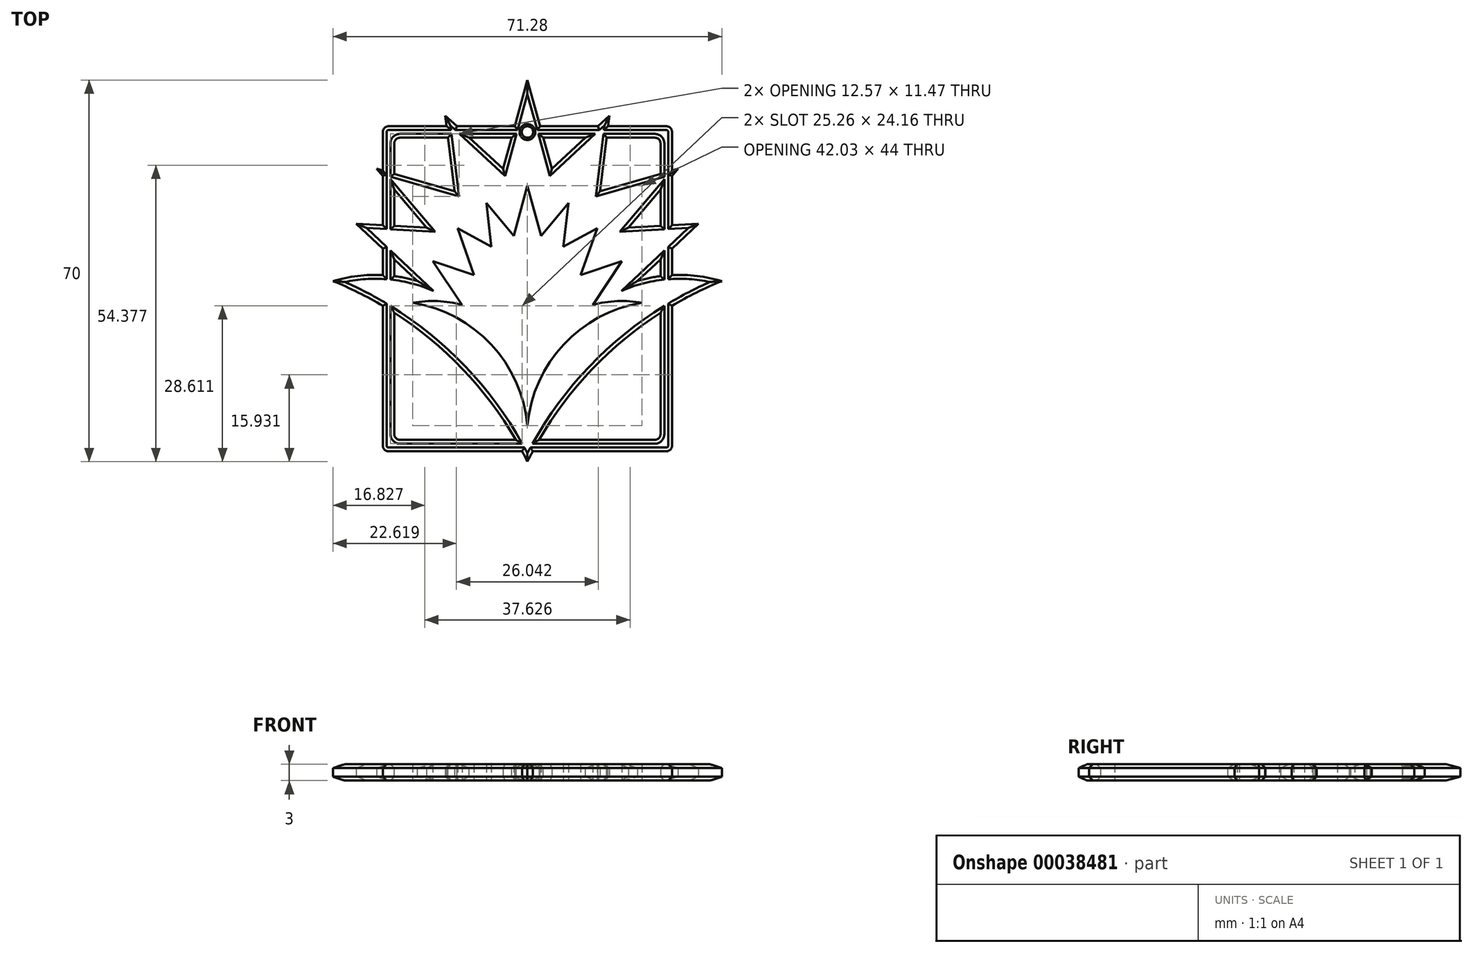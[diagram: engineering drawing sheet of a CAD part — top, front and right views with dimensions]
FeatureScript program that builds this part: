
annotation { "Feature Type Name" : "Feature", "Feature Type Description" : "" }
export const myFeature = defineFeature(function(context is Context, id is Id, definition is map)
    precondition{}
    {
        {
            var Q0;
            Q0=qCreatedBy(makeId("Top.planeOp"),FACE);
            var sketch = newSketch(context, id + "F0", { "sketchPlane" : qUnion([Q0])});
            skLineSegment(sketch, "E0", {"start": v(0, 33.84) * mm, "end": v(0, -36.16) * mm, "construction": true});
            skPoint(sketch, "E1", {"position": v(0, 26.84) * mm});
            skPoint(sketch, "E2", {"position": v(15.04, 27.3) * mm});
            skPoint(sketch, "E3", {"position": v(27.62, 17.57) * mm});
            skPoint(sketch, "E4", {"position": v(31.37, 7.5) * mm});
            skPoint(sketch, "E5", {"position": v(35.64, -3.05) * mm});
            skPoint(sketch, "E6", {"position": v(20.18, -3.02) * mm});
            skPoint(sketch, "E7", {"position": v(18.5, 6.8) * mm});
            skPoint(sketch, "E8", {"position": v(13.35, 13.45) * mm});
            skPoint(sketch, "E9", {"position": v(4.48, 17.54) * mm});
            skLineSegment(sketch, "E10", {"start": v(0, 33.84) * mm, "end": v(4.48, 17.54) * mm});
            skLineSegment(sketch, "E11", {"start": v(15.04, 27.3) * mm, "end": v(13.35, 13.45) * mm});
            skLineSegment(sketch, "E12", {"start": v(15.04, 27.3) * mm, "end": v(4.48, 17.54) * mm});
            skLineSegment(sketch, "E13", {"start": v(13.35, 13.45) * mm, "end": v(27.62, 17.57) * mm});
            skLineSegment(sketch, "E14", {"start": v(27.62, 17.57) * mm, "end": v(18.5, 6.8) * mm});
            skLineSegment(sketch, "E15", {"start": v(18.5, 6.8) * mm, "end": v(31.37, 7.5) * mm});
            skLineSegment(sketch, "E16", {"start": v(31.37, 7.5) * mm, "end": v(20.18, -3.02) * mm});
            skArc(sketch, "E17", {"start": v(35.64, -3.05) * mm, "mid": v(14.77, -16.33) * mm, "end": v(0, -36.16) * mm});
            skArc(sketch, "E18", {"start": v(35.64, -3.05) * mm, "mid": v(27.91, -1.91) * mm, "end": v(20.18, -3.02) * mm});
            skPoint(sketch, "E19.MirrorP", {"position": v(-4.48, 17.54) * mm});
            skPoint(sketch, "E20.MirrorP", {"position": v(-13.35, 13.45) * mm});
            skPoint(sketch, "E21.MirrorP", {"position": v(-15.04, 27.3) * mm});
            skPoint(sketch, "E22.MirrorP", {"position": v(-18.5, 6.8) * mm});
            skPoint(sketch, "E23.MirrorP", {"position": v(-20.18, -3.02) * mm});
            skPoint(sketch, "E24.MirrorP", {"position": v(-31.37, 7.5) * mm});
            skArc(sketch, "E25.MirrorCS", {"start": v(-35.64, -3.05) * mm, "mid": v(-27.91, -1.91) * mm, "end": v(-20.18, -3.02) * mm});
            skLineSegment(sketch, "E26.MirrorCS", {"start": v(0, 33.84) * mm, "end": v(-4.48, 17.54) * mm});
            skPoint(sketch, "E27.MirrorP", {"position": v(-35.64, -3.05) * mm});
            skLineSegment(sketch, "E28.MirrorCS", {"start": v(-15.04, 27.3) * mm, "end": v(-13.35, 13.45) * mm});
            skLineSegment(sketch, "E29.MirrorCS", {"start": v(-31.37, 7.5) * mm, "end": v(-20.18, -3.02) * mm});
            skPoint(sketch, "E30.MirrorP", {"position": v(-27.62, 17.57) * mm});
            skLineSegment(sketch, "E31.MirrorCS", {"start": v(-15.04, 27.3) * mm, "end": v(-4.48, 17.54) * mm});
            skArc(sketch, "E32.MirrorCS", {"start": v(-35.64, -3.05) * mm, "mid": v(-14.77, -16.33) * mm, "end": v(0, -36.16) * mm});
            skLineSegment(sketch, "E33.MirrorCS", {"start": v(-13.35, 13.45) * mm, "end": v(-27.62, 17.57) * mm});
            skLineSegment(sketch, "E34.MirrorCS", {"start": v(-27.62, 17.57) * mm, "end": v(-18.5, 6.8) * mm});
            skLineSegment(sketch, "E35.MirrorCS", {"start": v(-18.5, 6.8) * mm, "end": v(-31.37, 7.5) * mm});
            skSolve(sketch);
        }
        {
            var Q0;
            Q0=qCreatedBy(makeId("Top.planeOp"),FACE);
            var sketch = newSketch(context, id + "F1", { "sketchPlane" : qUnion([Q0])});
            skLineSegment(sketch, "E36", {"start": v(-11.97, -7.42) * mm, "end": v(-17.34, 0.6) * mm});
            skLineSegment(sketch, "E37", {"start": v(-17.34, 0.6) * mm, "end": v(-9.79, -1.93) * mm});
            skLineSegment(sketch, "E38", {"start": v(-9.79, -1.93) * mm, "end": v(-12.8, 6.64) * mm});
            skLineSegment(sketch, "E39", {"start": v(-12.8, 6.64) * mm, "end": v(-6.6, 3.28) * mm});
            skLineSegment(sketch, "E40", {"start": v(-6.6, 3.28) * mm, "end": v(-7.52, 11.26) * mm});
            skLineSegment(sketch, "E41", {"start": v(-7.52, 11.26) * mm, "end": v(-2.5, 5.26) * mm});
            skLineSegment(sketch, "E42", {"start": v(-2.5, 5.26) * mm, "end": v(0, 14.45) * mm});
            skArc(sketch, "E43", {"start": v(0, -29.55) * mm, "mid": v(-6.64, -14.68) * mm, "end": v(-21.02, -7.03) * mm});
            skLineSegment(sketch, "E44.MirrorCS", {"start": v(12.8, 6.64) * mm, "end": v(6.6, 3.28) * mm});
            skLineSegment(sketch, "E45.MirrorCS", {"start": v(6.6, 3.28) * mm, "end": v(7.52, 11.26) * mm});
            skLineSegment(sketch, "E46.MirrorCS", {"start": v(9.79, -1.93) * mm, "end": v(12.8, 6.64) * mm});
            skLineSegment(sketch, "E47.MirrorCS", {"start": v(17.34, 0.6) * mm, "end": v(9.79, -1.93) * mm});
            skLineSegment(sketch, "E48.MirrorCS", {"start": v(2.5, 5.26) * mm, "end": v(0, 14.45) * mm});
            skLineSegment(sketch, "E49.MirrorCS", {"start": v(11.97, -7.42) * mm, "end": v(17.34, 0.6) * mm});
            skLineSegment(sketch, "E50.MirrorCS", {"start": v(7.52, 11.26) * mm, "end": v(2.5, 5.26) * mm});
            skArc(sketch, "E51.MirrorCS", {"start": v(0, -29.55) * mm, "mid": v(6.64, -14.68) * mm, "end": v(21.02, -7.03) * mm});
            skArc(sketch, "E52", {"start": v(-11.97, -7.42) * mm, "mid": v(-16.47, -6.71) * mm, "end": v(-21.02, -7.03) * mm});
            skArc(sketch, "E53.MirrorCS", {"start": v(11.97, -7.42) * mm, "mid": v(16.47, -6.71) * mm, "end": v(21.02, -7.03) * mm});
            skSolve(sketch);
        }
        {
            var Q0;
            Q0=makeQuery(id+"F0.imprint","IMPRINT",FACE,{"disambiguationData":[TD([[makeQuery(id+"F0.imprint","IMPRINT",EDGE,{"derivedFrom":sQuery(id+"F0.wireOp",EDGE,"E10")}),-1.0]])]});
            extrude(context, id + "F2", {"entities" : qUnion([Q0]), "depth" : 3 * mm});
        }
        {
            var Q0;
            Q0=makeQuery(id+"F1.imprint","IMPRINT",FACE,{"disambiguationData":[TD([[makeQuery(id+"F1.imprint","IMPRINT",EDGE,{"derivedFrom":sQuery(id+"F1.wireOp",EDGE,"E36")}),-1.0]])]});
            extrude(context, id + "F3", {"entities" : qUnion([Q0]), "operationType" : NewBodyOperationType.REMOVE, "endBound" : BoundingType.UP_TO_NEXT, "depth" : 25 * mm});
        }
        {
            var Q0;
            Q0=qCreatedBy(makeId("Top.planeOp"),FACE);
            var sketch = newSketch(context, id + "F4", { "sketchPlane" : qUnion([Q0])});
            skLineSegment(sketch, "E54.bottom", {"start": v(-25.5, 25.35) * mm, "end": v(25.5, 25.35) * mm});
            skLineSegment(sketch, "E54.top", {"start": v(-25.5, -34.26) * mm, "end": v(25.5, -34.26) * mm});
            skLineSegment(sketch, "E54.left", {"start": v(-26.5, 24.35) * mm, "end": v(-26.5, -33.26) * mm});
            skLineSegment(sketch, "E54.right", {"start": v(26.5, 24.35) * mm, "end": v(26.5, -33.26) * mm});
            skPoint(sketch, "E55", {"position": v(0, 25.35) * mm});
            skLineSegment(sketch, "E56.0", {"start": v(24.4, 22.25) * mm, "end": v(24.4, -31.16) * mm});
            skLineSegment(sketch, "E56.1", {"start": v(-23.4, 23.25) * mm, "end": v(23.4, 23.25) * mm});
            skLineSegment(sketch, "E56.2", {"start": v(-24.4, 22.25) * mm, "end": v(-24.4, -31.16) * mm});
            skLineSegment(sketch, "E56.3", {"start": v(-23.4, -32.16) * mm, "end": v(23.4, -32.16) * mm});
            skPoint(sketch, "E57.visualSharp", {"position": v(-26.5, 25.35) * mm});
            skArc(sketch, "E57.filletArc", {"start": v(-25.5, 25.35) * mm, "mid": v(-26.2, 25.06) * mm, "end": v(-26.5, 24.35) * mm});
            skPoint(sketch, "E58.visualSharp", {"position": v(-24.4, 23.25) * mm});
            skArc(sketch, "E58.filletArc", {"start": v(-23.4, 23.25) * mm, "mid": v(-24.1, 22.96) * mm, "end": v(-24.4, 22.25) * mm});
            skPoint(sketch, "E59.visualSharp", {"position": v(-26.5, -34.26) * mm});
            skArc(sketch, "E59.filletArc", {"start": v(-26.5, -33.26) * mm, "mid": v(-26.2, -33.97) * mm, "end": v(-25.5, -34.26) * mm});
            skPoint(sketch, "E60.visualSharp", {"position": v(-24.4, -32.16) * mm});
            skArc(sketch, "E60.filletArc", {"start": v(-24.4, -31.16) * mm, "mid": v(-24.1, -31.87) * mm, "end": v(-23.4, -32.16) * mm});
            skPoint(sketch, "E61.visualSharp", {"position": v(24.4, -32.16) * mm});
            skArc(sketch, "E61.filletArc", {"start": v(23.4, -32.16) * mm, "mid": v(24.1, -31.87) * mm, "end": v(24.4, -31.16) * mm});
            skPoint(sketch, "E62.visualSharp", {"position": v(26.5, -34.26) * mm});
            skArc(sketch, "E62.filletArc", {"start": v(25.5, -34.26) * mm, "mid": v(26.2, -33.97) * mm, "end": v(26.5, -33.26) * mm});
            skPoint(sketch, "E63.visualSharp", {"position": v(24.4, 23.25) * mm});
            skArc(sketch, "E63.filletArc", {"start": v(24.4, 22.25) * mm, "mid": v(24.1, 22.96) * mm, "end": v(23.4, 23.25) * mm});
            skPoint(sketch, "E64.visualSharp", {"position": v(26.5, 25.35) * mm});
            skArc(sketch, "E64.filletArc", {"start": v(26.5, 24.35) * mm, "mid": v(26.2, 25.06) * mm, "end": v(25.5, 25.35) * mm});
            skSolve(sketch);
        }
        {
            var Q0;
            Q0=makeQuery(id+"F4.imprint","IMPRINT",FACE,{"disambiguationData":[TD([[makeQuery(id+"F4.imprint","IMPRINT",EDGE,{"derivedFrom":sQuery(id+"F4.wireOp",EDGE,"E54.bottom")}),-1.0]])]});
            var Q1;
            Q1=makeQuery(id+"F2.opExtrude","CAP_FACE",FACE,{"disambiguationData":[OSD([sQuery(id+"F0.wireOp",EDGE,"E10"),sQuery(id+"F0.wireOp",EDGE,"E11"),sQuery(id+"F0.wireOp",EDGE,"E12"),sQuery(id+"F0.wireOp",EDGE,"E13"),sQuery(id+"F0.wireOp",EDGE,"E14"),sQuery(id+"F0.wireOp",EDGE,"E15"),sQuery(id+"F0.wireOp",EDGE,"E16"),sQuery(id+"F0.wireOp",EDGE,"E17"),sQuery(id+"F0.wireOp",EDGE,"E18"),sQuery(id+"F0.wireOp",EDGE,"E25.MirrorCS"),sQuery(id+"F0.wireOp",EDGE,"E26.MirrorCS"),sQuery(id+"F0.wireOp",EDGE,"E28.MirrorCS"),sQuery(id+"F0.wireOp",EDGE,"E29.MirrorCS"),sQuery(id+"F0.wireOp",EDGE,"E31.MirrorCS"),sQuery(id+"F0.wireOp",EDGE,"E32.MirrorCS"),sQuery(id+"F0.wireOp",EDGE,"E33.MirrorCS"),sQuery(id+"F0.wireOp",EDGE,"E34.MirrorCS"),sQuery(id+"F0.wireOp",EDGE,"E35.MirrorCS")])],"isStart":false});
            extrude(context, id + "F5", {"entities" : qUnion([Q0]), "endBound" : BoundingType.UP_TO_SURFACE, "endBoundEntityFace" : qUnion([Q1]), "depth" : 25 * mm});
        }
        {
            var Q0;
            Q0=makeQuery(id+"F5.opExtrude","CAP_FACE",FACE,{"disambiguationData":[OSD([sQuery(id+"F4.wireOp",EDGE,"E54.bottom"),sQuery(id+"F4.wireOp",EDGE,"E54.top"),sQuery(id+"F4.wireOp",EDGE,"E54.left"),sQuery(id+"F4.wireOp",EDGE,"E54.right"),sQuery(id+"F4.wireOp",EDGE,"E56.0"),sQuery(id+"F4.wireOp",EDGE,"E56.1"),sQuery(id+"F4.wireOp",EDGE,"E56.2"),sQuery(id+"F4.wireOp",EDGE,"E56.3")])],"isStart":false});
            var Q1;
            Q1=makeQuery(id+"F5.opExtrude","CAP_FACE",FACE,{"disambiguationData":[OSD([sQuery(id+"F4.wireOp",EDGE,"E54.bottom"),sQuery(id+"F4.wireOp",EDGE,"E54.top"),sQuery(id+"F4.wireOp",EDGE,"E54.left"),sQuery(id+"F4.wireOp",EDGE,"E54.right"),sQuery(id+"F4.wireOp",EDGE,"E56.0"),sQuery(id+"F4.wireOp",EDGE,"E56.1"),sQuery(id+"F4.wireOp",EDGE,"E56.2"),sQuery(id+"F4.wireOp",EDGE,"E56.3")])],"isStart":true});
            chamfer(context, id + "F6", {"entities" : qUnion([Q0, Q1]), "width" : 0.7 * mm, "tangentPropagation" : true});
        }
        {
            var Q0;
            Q0=makeQuery(id+"F2.opExtrude","CAP_EDGE",EDGE,{"disambiguationData":[OSD([sQuery(id+"F0.wireOp",EDGE,"E32.MirrorCS")])],"isStart":false});
            var Q1;
            Q1=makeQuery(id+"F2.opExtrude","CAP_EDGE",EDGE,{"disambiguationData":[OSD([sQuery(id+"F0.wireOp",EDGE,"E25.MirrorCS")])],"isStart":false});
            var Q2;
            Q2=makeQuery(id+"F2.opExtrude","CAP_EDGE",EDGE,{"disambiguationData":[OSD([sQuery(id+"F0.wireOp",EDGE,"E29.MirrorCS")])],"isStart":false});
            var Q3;
            Q3=makeQuery(id+"F2.opExtrude","CAP_EDGE",EDGE,{"disambiguationData":[OSD([sQuery(id+"F0.wireOp",EDGE,"E35.MirrorCS")])],"isStart":false});
            var Q4;
            Q4=makeQuery(id+"F2.opExtrude","CAP_EDGE",EDGE,{"disambiguationData":[OSD([sQuery(id+"F0.wireOp",EDGE,"E34.MirrorCS")])],"isStart":false});
            var Q5;
            Q5=makeQuery(id+"F2.opExtrude","CAP_EDGE",EDGE,{"disambiguationData":[OSD([sQuery(id+"F0.wireOp",EDGE,"E33.MirrorCS")])],"isStart":false});
            var Q6;
            Q6=makeQuery(id+"F2.opExtrude","CAP_EDGE",EDGE,{"disambiguationData":[OSD([sQuery(id+"F0.wireOp",EDGE,"E28.MirrorCS")])],"isStart":false});
            var Q7;
            Q7=makeQuery(id+"F2.opExtrude","CAP_EDGE",EDGE,{"disambiguationData":[OSD([sQuery(id+"F0.wireOp",EDGE,"E31.MirrorCS")])],"isStart":false});
            var Q8;
            Q8=makeQuery(id+"F2.opExtrude","CAP_EDGE",EDGE,{"disambiguationData":[OSD([sQuery(id+"F0.wireOp",EDGE,"E26.MirrorCS")])],"isStart":false});
            var Q9;
            Q9=makeQuery(id+"F2.opExtrude","CAP_EDGE",EDGE,{"disambiguationData":[OSD([sQuery(id+"F0.wireOp",EDGE,"E10")])],"isStart":false});
            var Q10;
            Q10=makeQuery(id+"F2.opExtrude","CAP_EDGE",EDGE,{"disambiguationData":[OSD([sQuery(id+"F0.wireOp",EDGE,"E12")])],"isStart":false});
            var Q11;
            Q11=makeQuery(id+"F2.opExtrude","CAP_EDGE",EDGE,{"disambiguationData":[OSD([sQuery(id+"F0.wireOp",EDGE,"E11")])],"isStart":false});
            var Q12;
            Q12=makeQuery(id+"F2.opExtrude","CAP_EDGE",EDGE,{"disambiguationData":[OSD([sQuery(id+"F0.wireOp",EDGE,"E13")])],"isStart":false});
            var Q13;
            Q13=makeQuery(id+"F2.opExtrude","CAP_EDGE",EDGE,{"disambiguationData":[OSD([sQuery(id+"F0.wireOp",EDGE,"E14")])],"isStart":false});
            var Q14;
            Q14=makeQuery(id+"F2.opExtrude","CAP_EDGE",EDGE,{"disambiguationData":[OSD([sQuery(id+"F0.wireOp",EDGE,"E15")])],"isStart":false});
            var Q15;
            Q15=makeQuery(id+"F2.opExtrude","CAP_EDGE",EDGE,{"disambiguationData":[OSD([sQuery(id+"F0.wireOp",EDGE,"E16")])],"isStart":false});
            var Q16;
            Q16=makeQuery(id+"F2.opExtrude","CAP_EDGE",EDGE,{"disambiguationData":[OSD([sQuery(id+"F0.wireOp",EDGE,"E18")])],"isStart":false});
            var Q17;
            Q17=makeQuery(id+"F2.opExtrude","CAP_EDGE",EDGE,{"disambiguationData":[OSD([sQuery(id+"F0.wireOp",EDGE,"E17")])],"isStart":false});
            chamfer(context, id + "F7", {"entities" : qUnion([Q0, Q1, Q2, Q3, Q4, Q5, Q6, Q7, Q8, Q9, Q10, Q11, Q12, Q13, Q14, Q15, Q16, Q17]), "width" : 0.7 * mm});
        }
        {
            var Q0;
            Q0=makeQuery(id+"F2.opExtrude","CAP_EDGE",EDGE,{"disambiguationData":[OSD([sQuery(id+"F0.wireOp",EDGE,"E17")])],"isStart":true});
            var Q1;
            Q1=makeQuery(id+"F2.opExtrude","CAP_EDGE",EDGE,{"disambiguationData":[OSD([sQuery(id+"F0.wireOp",EDGE,"E18")])],"isStart":true});
            var Q2;
            Q2=makeQuery(id+"F2.opExtrude","CAP_EDGE",EDGE,{"disambiguationData":[OSD([sQuery(id+"F0.wireOp",EDGE,"E16")])],"isStart":true});
            var Q3;
            Q3=makeQuery(id+"F2.opExtrude","CAP_EDGE",EDGE,{"disambiguationData":[OSD([sQuery(id+"F0.wireOp",EDGE,"E15")])],"isStart":true});
            var Q4;
            Q4=makeQuery(id+"F2.opExtrude","CAP_EDGE",EDGE,{"disambiguationData":[OSD([sQuery(id+"F0.wireOp",EDGE,"E14")])],"isStart":true});
            var Q5;
            Q5=makeQuery(id+"F2.opExtrude","CAP_EDGE",EDGE,{"disambiguationData":[OSD([sQuery(id+"F0.wireOp",EDGE,"E13")])],"isStart":true});
            var Q6;
            Q6=makeQuery(id+"F2.opExtrude","CAP_EDGE",EDGE,{"disambiguationData":[OSD([sQuery(id+"F0.wireOp",EDGE,"E11")])],"isStart":true});
            var Q7;
            Q7=makeQuery(id+"F2.opExtrude","CAP_EDGE",EDGE,{"disambiguationData":[OSD([sQuery(id+"F0.wireOp",EDGE,"E12")])],"isStart":true});
            var Q8;
            Q8=makeQuery(id+"F2.opExtrude","CAP_EDGE",EDGE,{"disambiguationData":[OSD([sQuery(id+"F0.wireOp",EDGE,"E10")])],"isStart":true});
            var Q9;
            Q9=makeQuery(id+"F2.opExtrude","CAP_EDGE",EDGE,{"disambiguationData":[OSD([sQuery(id+"F0.wireOp",EDGE,"E26.MirrorCS")])],"isStart":true});
            var Q10;
            Q10=makeQuery(id+"F2.opExtrude","CAP_EDGE",EDGE,{"disambiguationData":[OSD([sQuery(id+"F0.wireOp",EDGE,"E31.MirrorCS")])],"isStart":true});
            var Q11;
            Q11=makeQuery(id+"F2.opExtrude","CAP_EDGE",EDGE,{"disambiguationData":[OSD([sQuery(id+"F0.wireOp",EDGE,"E28.MirrorCS")])],"isStart":true});
            var Q12;
            Q12=makeQuery(id+"F2.opExtrude","CAP_EDGE",EDGE,{"disambiguationData":[OSD([sQuery(id+"F0.wireOp",EDGE,"E33.MirrorCS")])],"isStart":true});
            var Q13;
            Q13=makeQuery(id+"F2.opExtrude","CAP_EDGE",EDGE,{"disambiguationData":[OSD([sQuery(id+"F0.wireOp",EDGE,"E34.MirrorCS")])],"isStart":true});
            var Q14;
            Q14=makeQuery(id+"F2.opExtrude","CAP_EDGE",EDGE,{"disambiguationData":[OSD([sQuery(id+"F0.wireOp",EDGE,"E35.MirrorCS")])],"isStart":true});
            var Q15;
            Q15=makeQuery(id+"F2.opExtrude","CAP_EDGE",EDGE,{"disambiguationData":[OSD([sQuery(id+"F0.wireOp",EDGE,"E29.MirrorCS")])],"isStart":true});
            var Q16;
            Q16=makeQuery(id+"F2.opExtrude","CAP_EDGE",EDGE,{"disambiguationData":[OSD([sQuery(id+"F0.wireOp",EDGE,"E25.MirrorCS")])],"isStart":true});
            var Q17;
            Q17=makeQuery(id+"F2.opExtrude","CAP_EDGE",EDGE,{"disambiguationData":[OSD([sQuery(id+"F0.wireOp",EDGE,"E32.MirrorCS")])],"isStart":true});
            chamfer(context, id + "F8", {"entities" : qUnion([Q0, Q1, Q2, Q3, Q4, Q5, Q6, Q7, Q8, Q9, Q10, Q11, Q12, Q13, Q14, Q15, Q16, Q17]), "width" : 0.7 * mm, "tangentPropagation" : true});
        }
        {
            var Q0;
            Q0=makeQuery(id+"F2.opExtrude","SWEPT_BODY",BODY,{"disambiguationData":[OSD([sQuery(id+"F0.wireOp",EDGE,"E10"),sQuery(id+"F0.wireOp",EDGE,"E11"),sQuery(id+"F0.wireOp",EDGE,"E12"),sQuery(id+"F0.wireOp",EDGE,"E13"),sQuery(id+"F0.wireOp",EDGE,"E14"),sQuery(id+"F0.wireOp",EDGE,"E15"),sQuery(id+"F0.wireOp",EDGE,"E16"),sQuery(id+"F0.wireOp",EDGE,"E17"),sQuery(id+"F0.wireOp",EDGE,"E18"),sQuery(id+"F0.wireOp",EDGE,"E25.MirrorCS"),sQuery(id+"F0.wireOp",EDGE,"E26.MirrorCS"),sQuery(id+"F0.wireOp",EDGE,"E28.MirrorCS"),sQuery(id+"F0.wireOp",EDGE,"E29.MirrorCS"),sQuery(id+"F0.wireOp",EDGE,"E31.MirrorCS"),sQuery(id+"F0.wireOp",EDGE,"E32.MirrorCS"),sQuery(id+"F0.wireOp",EDGE,"E33.MirrorCS"),sQuery(id+"F0.wireOp",EDGE,"E34.MirrorCS"),sQuery(id+"F0.wireOp",EDGE,"E35.MirrorCS")])]});
            var Q1;
            Q1=makeQuery(id+"F5.opExtrude","SWEPT_BODY",BODY,{"disambiguationData":[OSD([sQuery(id+"F4.wireOp",EDGE,"E54.bottom"),sQuery(id+"F4.wireOp",EDGE,"E54.top"),sQuery(id+"F4.wireOp",EDGE,"E54.left"),sQuery(id+"F4.wireOp",EDGE,"E54.right"),sQuery(id+"F4.wireOp",EDGE,"E56.0"),sQuery(id+"F4.wireOp",EDGE,"E56.1"),sQuery(id+"F4.wireOp",EDGE,"E56.2"),sQuery(id+"F4.wireOp",EDGE,"E56.3")])]});
            booleanBodies(context, id + "F9", {"operationType" : BooleanOperationType.UNION, "tools" : qUnion([Q0, Q1])});
        }
        {
            var Q0;
            Q0=qCreatedBy(makeId("Top.planeOp"),FACE);
            var sketch = newSketch(context, id + "F10", { "sketchPlane" : qUnion([Q0])});
            skCircle(sketch, "E65", {"center": v(0, 24.3) * mm, "radius": 1.05 * mm});
            skLineSegment(sketch, "E66.0", {"start": v(-25.5, 25.35) * mm, "end": v(25.5, 25.35) * mm, "construction": true});
            skLineSegment(sketch, "E66.1", {"start": v(-23.4, 23.25) * mm, "end": v(23.4, 23.25) * mm, "construction": true});
            skLineSegment(sketch, "E67", {"start": v(0, 25.35) * mm, "end": v(0, 23.25) * mm, "construction": true});
            skSolve(sketch);
        }
        {
            var Q0;
            Q0 = qSketchRegion(id + "F10", true);
            var Q1;
            Q1=makeQuery(id+"F9.opBoolean","MERGE",FACE,{"derivedFrom":[makeQuery(id+"F5.opExtrude","CAP_FACE",FACE,{"disambiguationData":[OSD([sQuery(id+"F4.wireOp",EDGE,"E54.bottom"),sQuery(id+"F4.wireOp",EDGE,"E54.top"),sQuery(id+"F4.wireOp",EDGE,"E54.left"),sQuery(id+"F4.wireOp",EDGE,"E54.right"),sQuery(id+"F4.wireOp",EDGE,"E56.0"),sQuery(id+"F4.wireOp",EDGE,"E56.1"),sQuery(id+"F4.wireOp",EDGE,"E56.2"),sQuery(id+"F4.wireOp",EDGE,"E56.3")])],"isStart":false}),makeQuery(id+"F2.opExtrude","CAP_FACE",FACE,{"disambiguationData":[OSD([sQuery(id+"F0.wireOp",EDGE,"E10"),sQuery(id+"F0.wireOp",EDGE,"E11"),sQuery(id+"F0.wireOp",EDGE,"E12"),sQuery(id+"F0.wireOp",EDGE,"E13"),sQuery(id+"F0.wireOp",EDGE,"E14"),sQuery(id+"F0.wireOp",EDGE,"E15"),sQuery(id+"F0.wireOp",EDGE,"E16"),sQuery(id+"F0.wireOp",EDGE,"E17"),sQuery(id+"F0.wireOp",EDGE,"E18"),sQuery(id+"F0.wireOp",EDGE,"E25.MirrorCS"),sQuery(id+"F0.wireOp",EDGE,"E26.MirrorCS"),sQuery(id+"F0.wireOp",EDGE,"E28.MirrorCS"),sQuery(id+"F0.wireOp",EDGE,"E29.MirrorCS"),sQuery(id+"F0.wireOp",EDGE,"E31.MirrorCS"),sQuery(id+"F0.wireOp",EDGE,"E32.MirrorCS"),sQuery(id+"F0.wireOp",EDGE,"E33.MirrorCS"),sQuery(id+"F0.wireOp",EDGE,"E34.MirrorCS"),sQuery(id+"F0.wireOp",EDGE,"E35.MirrorCS")])],"isStart":false})]});
            extrude(context, id + "F11", {"entities" : qUnion([Q0]), "operationType" : NewBodyOperationType.REMOVE, "endBound" : BoundingType.UP_TO_SURFACE, "endBoundEntityFace" : qUnion([Q1]), "depth" : 25 * mm});
        }
        {
            var Q0;
            Q0=makeQuery(id+"F11.boolean.opBoolean","COPY",FACE,{"derivedFrom":makeQuery(id+"F11.opExtrude","SWEPT_FACE",FACE,{"disambiguationData":[OSD([sQuery(id+"F10.wireOp",EDGE,"E65")])]})});
            chamfer(context, id + "F12", {"entities" : qUnion([Q0]), "width" : .4 * mm, "tangentPropagation" : true});
        }
    });
